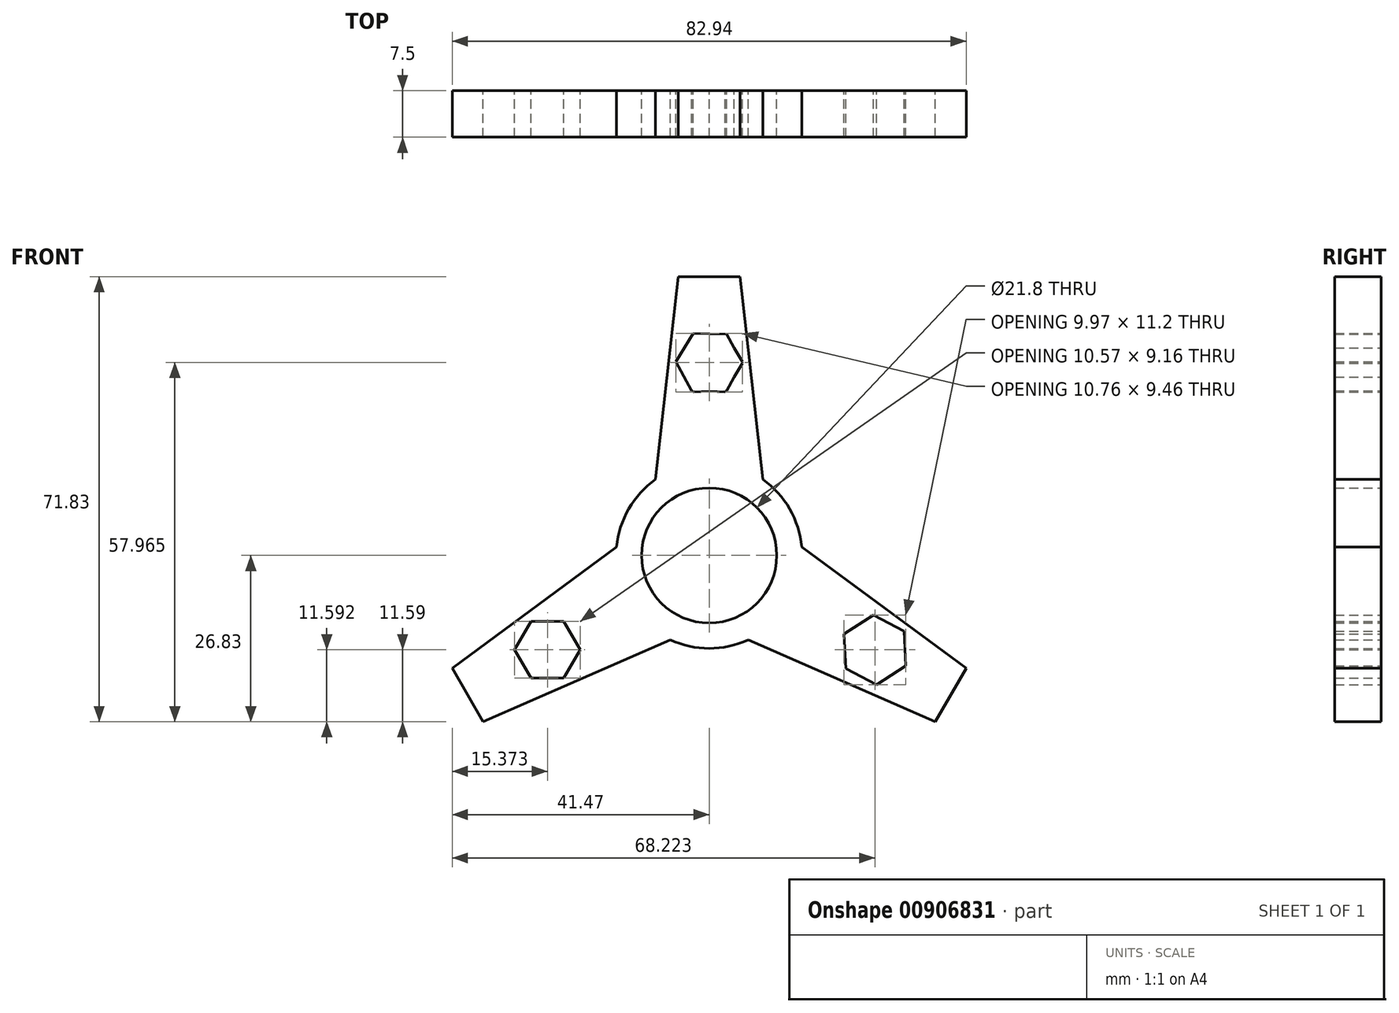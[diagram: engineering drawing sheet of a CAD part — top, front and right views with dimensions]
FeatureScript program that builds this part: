
annotation { "Feature Type Name" : "Feature", "Feature Type Description" : "" }
export const myFeature = defineFeature(function(context is Context, id is Id, definition is map)
    precondition{}
    {
        {
            var Q0;
            Q0=qCreatedBy(makeId("Front.planeOp"),FACE);
            var sketch = newSketch(context, id + "F0", { "sketchPlane" : qUnion([Q0])});
            skCircle(sketch, "E0", {"center": v(0, 0) * mm, "radius": 10.9 * mm});
            skCircle(sketch, "E1", {"center": v(0, 0) * mm, "radius": 15 * mm});
            skLineSegment(sketch, "E2", {"start": v(0, 45) * mm, "end": v(-5, 45) * mm});
            skLineSegment(sketch, "E3", {"start": v(-5, 45) * mm, "end": v(-8.65, 12.25) * mm});
            skLineSegment(sketch, "E4.MirrorCS", {"start": v(5, 45) * mm, "end": v(8.65, 12.25) * mm});
            skLineSegment(sketch, "E5.MirrorCS", {"start": v(0, 45) * mm, "end": v(5, 45) * mm});
            skLineSegment(sketch, "E6.1.0", {"start": v(-36.47, -26.83) * mm, "end": v(-6.28, -13.62) * mm});
            skLineSegment(sketch, "E6.1.1", {"start": v(-38.97, -22.5) * mm, "end": v(-36.47, -26.83) * mm});
            skLineSegment(sketch, "E6.1.2", {"start": v(-38.97, -22.5) * mm, "end": v(-41.47, -18.17) * mm});
            skLineSegment(sketch, "E6.1.3", {"start": v(-41.47, -18.17) * mm, "end": v(-14.94, 1.37) * mm});
            skLineSegment(sketch, "E6.2.0", {"start": v(41.47, -18.17) * mm, "end": v(14.94, 1.37) * mm});
            skLineSegment(sketch, "E6.2.1", {"start": v(38.97, -22.5) * mm, "end": v(41.47, -18.17) * mm});
            skLineSegment(sketch, "E6.2.2", {"start": v(38.97, -22.5) * mm, "end": v(36.47, -26.83) * mm});
            skLineSegment(sketch, "E6.2.3", {"start": v(36.47, -26.83) * mm, "end": v(6.28, -13.62) * mm});
            skPoint(sketch, "E7.0.midPoint", {"position": v(-4.82, 23.26) * mm});
            skLineSegment(sketch, "E8.0", {"start": v(5.38, 31.27) * mm, "end": v(2.8, 26.55) * mm});
            skLineSegment(sketch, "E8.1", {"start": v(2.8, 26.55) * mm, "end": v(-2.57, 26.4) * mm});
            skLineSegment(sketch, "E8.2", {"start": v(-2.57, 26.4) * mm, "end": v(-5.38, 31) * mm});
            skLineSegment(sketch, "E8.5", {"start": v(2.57, 35.86) * mm, "end": v(5.38, 31.27) * mm});
            skPoint(sketch, "E8.0.midPoint", {"position": v(4.1, 28.9) * mm});
            skLineSegment(sketch, "E9.MirrorCS", {"start": v(5.38, 31) * mm, "end": v(2.8, 35.73) * mm});
            skLineSegment(sketch, "E10.MirrorCS", {"start": v(-5.38, 31.27) * mm, "end": v(-2.8, 26.55) * mm});
            skLineSegment(sketch, "E11.MirrorCS", {"start": v(2.57, 26.4) * mm, "end": v(5.38, 31) * mm});
            skLineSegment(sketch, "E12.MirrorCS", {"start": v(-2.8, 26.55) * mm, "end": v(2.57, 26.4) * mm});
            skLineSegment(sketch, "E13.MirrorCS", {"start": v(-2.57, 35.86) * mm, "end": v(-5.38, 31.27) * mm});
            skLineSegment(sketch, "E14.MirrorCS", {"start": v(2.8, 35.73) * mm, "end": v(-2.57, 35.86) * mm});
            skLineSegment(sketch, "E15.0", {"start": v(-28.74, -10.66) * mm, "end": v(-23.45, -10.66) * mm});
            skLineSegment(sketch, "E15.1", {"start": v(-23.45, -10.66) * mm, "end": v(-20.81, -15.24) * mm});
            skLineSegment(sketch, "E15.2", {"start": v(-20.81, -15.24) * mm, "end": v(-23.45, -19.82) * mm});
            skLineSegment(sketch, "E15.3", {"start": v(-23.45, -19.82) * mm, "end": v(-28.74, -19.82) * mm});
            skLineSegment(sketch, "E15.4", {"start": v(-28.74, -19.82) * mm, "end": v(-31.38, -15.24) * mm});
            skLineSegment(sketch, "E15.5", {"start": v(-31.38, -15.24) * mm, "end": v(-28.74, -10.66) * mm});
            skPoint(sketch, "E15.0.midPoint", {"position": v(-26.1, -10.66) * mm});
            skPoint(sketch, "E16.0.midPoint", {"position": v(14.65, -7.47) * mm});
            skLineSegment(sketch, "E17.0", {"start": v(27.02, -20.84) * mm, "end": v(22.04, -18.27) * mm});
            skLineSegment(sketch, "E17.1", {"start": v(22.04, -18.27) * mm, "end": v(21.77, -12.67) * mm});
            skLineSegment(sketch, "E17.2", {"start": v(21.77, -12.67) * mm, "end": v(26.48, -9.64) * mm});
            skLineSegment(sketch, "E17.3", {"start": v(26.48, -9.64) * mm, "end": v(31.47, -12.2) * mm});
            skLineSegment(sketch, "E17.4", {"start": v(31.47, -12.2) * mm, "end": v(31.74, -17.8) * mm});
            skLineSegment(sketch, "E17.5", {"start": v(31.74, -17.8) * mm, "end": v(27.02, -20.84) * mm});
            skPoint(sketch, "E17.0.midPoint", {"position": v(24.53, -19.55) * mm});
            skSolve(sketch);
        }
        {
            var Q0;
            {var subQ1=sQuery(id+"F0.wireOp",EDGE,"E6.2.0");Q0=makeQuery(id+"F0.imprint","IMPRINT",FACE,{"disambiguationData":[TD([[makeQuery(id+"F0.imprint","IMPRINT",EDGE,{"derivedFrom":subQ1}),1.0]])]});}
            var Q1;
            {var subQ0=sQuery(id+"F0.wireOp",EDGE,"E6.1.0");Q1=makeQuery(id+"F0.imprint","IMPRINT",FACE,{"disambiguationData":[TD([[makeQuery(id+"F0.imprint","IMPRINT",EDGE,{"derivedFrom":subQ0}),1.0]])]});}
            var Q2;
            Q2=makeQuery(id+"F0.imprint","IMPRINT",FACE,{"disambiguationData":[TD([[makeQuery(id+"F0.imprint","IMPRINT",EDGE,{"derivedFrom":sQuery(id+"F0.wireOp",EDGE,"E2")}),1.0]])]});
            var Q3;
            Q3=makeQuery(id+"F0.imprint","IMPRINT",FACE,{"disambiguationData":[TD([[makeQuery(id+"F0.imprint","IMPRINT",EDGE,{"derivedFrom":sQuery(id+"F0.wireOp",EDGE,"E0")}),-1.0]])]});
            var Q4;
            Q4=makeQuery(id+"F0.imprint","IMPRINT",FACE,{"disambiguationData":[TD([[makeQuery(id+"F0.imprint","IMPRINT",EDGE,{"derivedFrom":sQuery(id+"F0.wireOp",EDGE,"E6.1.2")}),-1.0]])]});
            var Q5;
            Q5=makeQuery(id+"F0.imprint","IMPRINT",FACE,{"disambiguationData":[TD([[makeQuery(id+"F0.imprint","IMPRINT",EDGE,{"derivedFrom":sQuery(id+"F0.wireOp",EDGE,"E0")}),1.0]])]});
            var Q6;
            Q6=makeQuery(id+"F0.imprint","IMPRINT",FACE,{"disambiguationData":[TD([[makeQuery(id+"F0.imprint","IMPRINT",EDGE,{"derivedFrom":sQuery(id+"F0.wireOp",EDGE,"E5.MirrorCS")}),-1.0]])]});
            var Q7;
            Q7=makeQuery(id+"F0.imprint","IMPRINT",FACE,{"disambiguationData":[TD([[makeQuery(id+"F0.imprint","IMPRINT",EDGE,{"derivedFrom":sQuery(id+"F0.wireOp",EDGE,"E6.2.2")}),-1.0]])]});
            extrude(context, id + "F1", {"entities" : qUnion([Q0, Q1, Q2, Q3, Q4, Q5, Q6, Q7]), "endBound" : BoundingType.SYMMETRIC, "depth" : 7.5 * mm, "offsetDistance" : 25 * mm});
        }
    });
